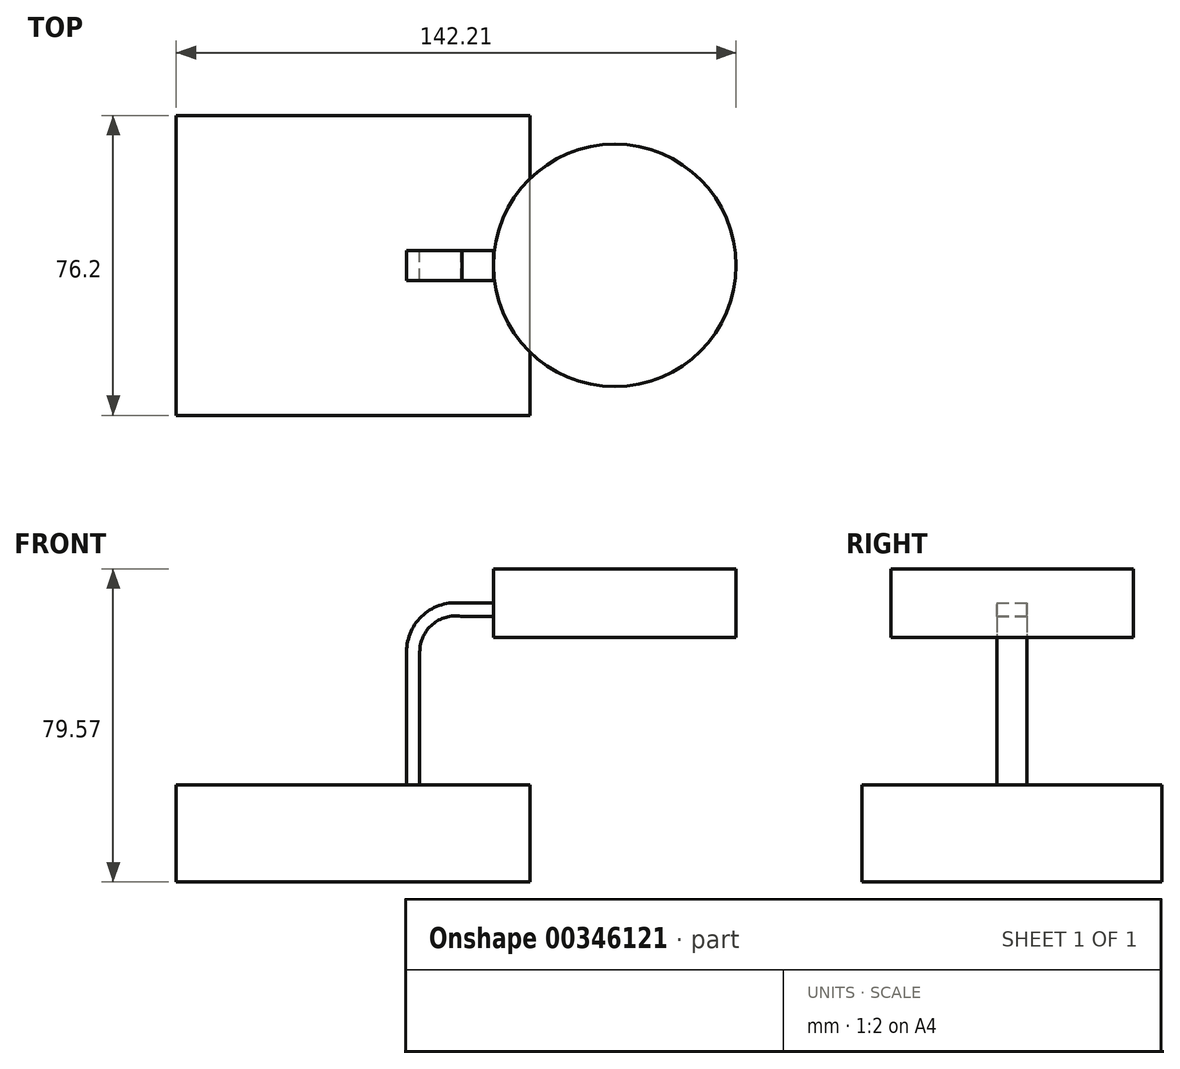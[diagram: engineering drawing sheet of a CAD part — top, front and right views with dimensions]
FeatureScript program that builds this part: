
annotation { "Feature Type Name" : "Feature", "Feature Type Description" : "" }
export const myFeature = defineFeature(function(context is Context, id is Id, definition is map)
    precondition{}
    {
        {
            var Q0;
            Q0=qCreatedBy(makeId("Front.planeOp"),FACE);
            var sketch = newSketch(context, id + "F0", { "sketchPlane" : qUnion([Q0])});
            skLineSegment(sketch, "E0.bottom", {"start": v(44.92, -12.32) * mm, "end": v(-44.92, -12.32) * mm});
            skLineSegment(sketch, "E0.top", {"start": v(44.92, 12.32) * mm, "end": v(-44.92, 12.32) * mm});
            skLineSegment(sketch, "E0.left", {"start": v(44.92, -12.32) * mm, "end": v(44.92, 12.32) * mm});
            skLineSegment(sketch, "E0.right", {"start": v(-44.92, -12.32) * mm, "end": v(-44.92, 12.32) * mm});
            skPoint(sketch, "E0.middle", {"position": v(0, 0) * mm});
            skLineSegment(sketch, "E1.bottom", {"start": v(66.48, 49.8) * mm, "end": v(35.68, 49.8) * mm});
            skLineSegment(sketch, "E1.top", {"start": v(66.48, 67.25) * mm, "end": v(35.68, 67.25) * mm});
            skLineSegment(sketch, "E1.left", {"start": v(66.48, 49.8) * mm, "end": v(66.48, 67.25) * mm});
            skLineSegment(sketch, "E1.right", {"start": v(35.68, 49.8) * mm, "end": v(35.68, 67.25) * mm});
            skPoint(sketch, "E1.middle", {"position": v(51.08, 58.53) * mm});
            skLineSegment(sketch, "E2", {"start": v(16.94, 12.32) * mm, "end": v(16.94, 46.2) * mm});
            skArc(sketch, "E3", {"start": v(16.94, 46.2) * mm, "mid": v(20.13, 53.12) * mm, "end": v(27.47, 55.2) * mm});
            skLineSegment(sketch, "E4", {"start": v(27.47, 55.2) * mm, "end": v(35.68, 55.2) * mm});
            skLineSegment(sketch, "E5.0", {"start": v(27.7, 58.53) * mm, "end": v(35.68, 58.53) * mm});
            skArc(sketch, "E5.1", {"start": v(13.6, 46.2) * mm, "mid": v(17.86, 55.57) * mm, "end": v(27.7, 58.53) * mm});
            skLineSegment(sketch, "E5.2", {"start": v(13.6, 12.32) * mm, "end": v(13.6, 46.2) * mm});
            skSolve(sketch);
        }
        {
            var Q0;
            Q0=makeQuery(id+"F0.imprint","IMPRINT",FACE,{"disambiguationData":[TD([[makeQuery(id+"F0.imprint","IMPRINT",EDGE,{"derivedFrom":sQuery(id+"F0.wireOp",EDGE,"E0.bottom")}),-1.0]])]});
            extrude(context, id + "F1", {"entities" : qUnion([Q0]), "endBound" : BoundingType.SYMMETRIC, "depth" : 76.2 * mm});
        }
        {
            var Q0;
            {var subQ1=sQuery(id+"F0.wireOp",EDGE,"E1.bottom");Q0=makeQuery(id+"F0.imprint","IMPRINT",FACE,{"disambiguationData":[TD([[makeQuery(id+"F0.imprint","IMPRINT",EDGE,{"derivedFrom":subQ1}),-1.0]])]});}
            var Q1;
            Q1=sQuery(id+"F0.wireOp",EDGE,"E1.left");
            revolve(context, id + "F2", {"entities" : qUnion([Q0]), "axis" : qUnion([Q1]), "revolveType" : RevolveType.FULL});
        }
        {
            var Q0;
            {var subQ0=sQuery(id+"F0.wireOp",EDGE,"E2");Q0=makeQuery(id+"F0.imprint","IMPRINT",FACE,{"disambiguationData":[TD([[makeQuery(id+"F0.imprint","IMPRINT",EDGE,{"derivedFrom":subQ0}),1.0]])]});}
            extrude(context, id + "F3", {"entities" : qUnion([Q0]), "endBound" : BoundingType.SYMMETRIC, "depth" : 7.62 * mm});
        }
    });
